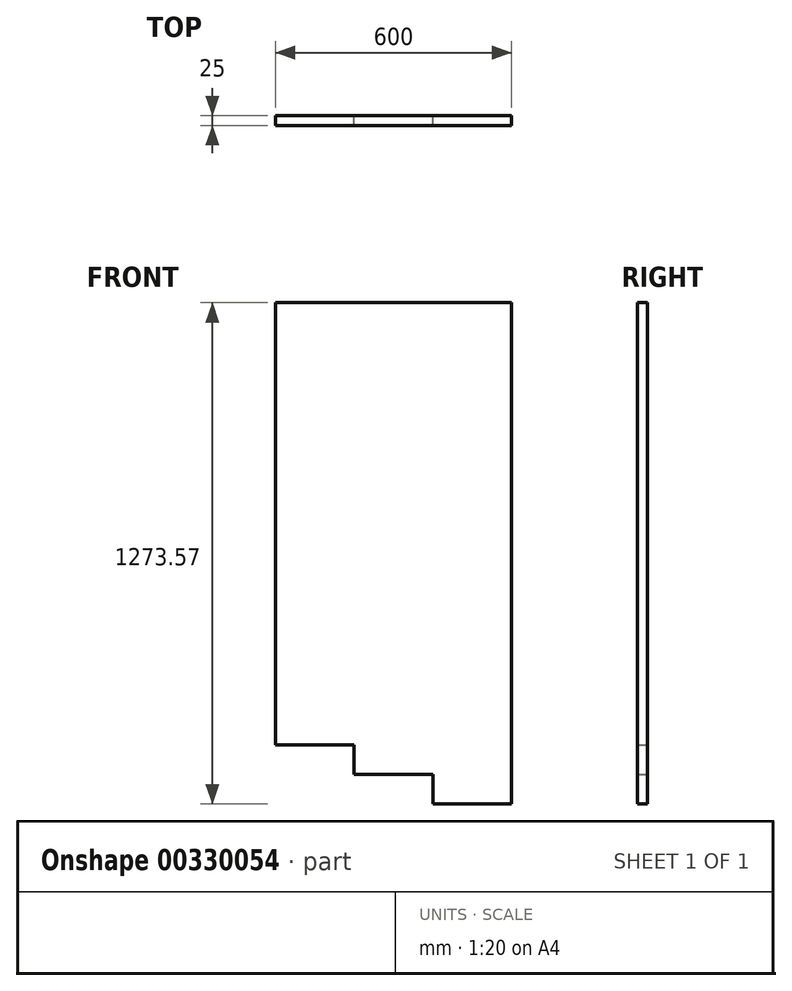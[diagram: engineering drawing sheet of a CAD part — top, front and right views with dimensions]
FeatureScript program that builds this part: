
annotation { "Feature Type Name" : "Feature", "Feature Type Description" : "" }
export const myFeature = defineFeature(function(context is Context, id is Id, definition is map)
    precondition{}
    {
        {
            var Q0;
            Q0=qCreatedBy(makeId("Front.planeOp"),FACE);
            var sketch = newSketch(context, id + "F0", { "sketchPlane" : qUnion([Q0])});
            skLineSegment(sketch, "E0.MirrorCS", {"start": v(296.77, -607.63) * mm, "end": v(296.77, -1731.2) * mm});
            skLineSegment(sketch, "E1.MirrorCS", {"start": v(496.77, -1731.2) * mm, "end": v(496.77, -1806.2) * mm});
            skLineSegment(sketch, "E2.MirrorCS", {"start": v(696.77, -1806.2) * mm, "end": v(696.77, -1881.2) * mm});
            skLineSegment(sketch, "E3.MirrorCS", {"start": v(296.77, -1731.2) * mm, "end": v(496.77, -1731.2) * mm});
            skLineSegment(sketch, "E4.MirrorCS", {"start": v(496.77, -1806.2) * mm, "end": v(696.77, -1806.2) * mm});
            skLineSegment(sketch, "E5.MirrorCS", {"start": v(896.77, -1881.2) * mm, "end": v(896.77, -607.63) * mm});
            skLineSegment(sketch, "E6.MirrorCS", {"start": v(696.77, -1881.2) * mm, "end": v(896.77, -1881.2) * mm});
            skLineSegment(sketch, "E7.MirrorCS", {"start": v(896.77, -607.63) * mm, "end": v(296.77, -607.63) * mm});
            skSolve(sketch);
        }
        {
            var Q0;
            Q0=makeQuery(id+"F0.imprint","IMPRINT",FACE,{"disambiguationData":[TD([[makeQuery(id+"F0.imprint","IMPRINT",EDGE,{"derivedFrom":sQuery(id+"F0.wireOp",EDGE,"E0.MirrorCS")}),1.0]])]});
            extrude(context, id + "F1", {"entities" : qUnion([Q0]), "depth" : 25 * mm});
        }
    });
